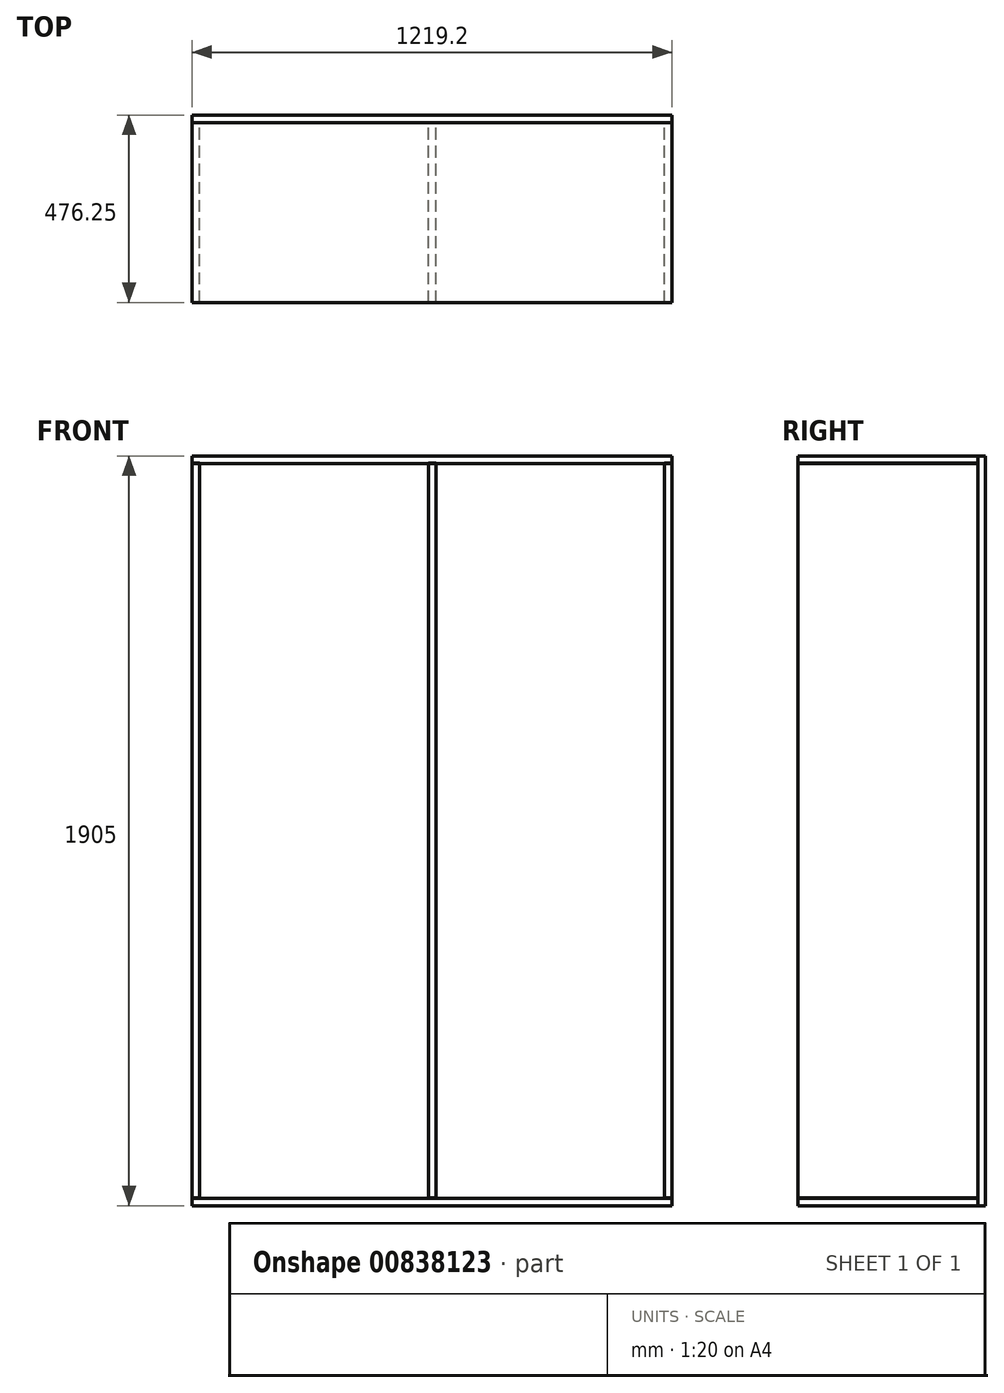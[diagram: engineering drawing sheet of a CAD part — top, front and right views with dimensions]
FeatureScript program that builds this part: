
annotation { "Feature Type Name" : "Feature", "Feature Type Description" : "" }
export const myFeature = defineFeature(function(context is Context, id is Id, definition is map)
    precondition{}
    {
        {
            var Q0;
            Q0=qCreatedBy(makeId("Front.planeOp"),FACE);
            var sketch = newSketch(context, id + "F0", { "sketchPlane" : qUnion([Q0])});
            skLineSegment(sketch, "E0.bottom", {"start": v(0, 0) * mm, "end": v(1219.2, 0) * mm});
            skLineSegment(sketch, "E0.top", {"start": v(0, 1905) * mm, "end": v(1219.2, 1905) * mm});
            skLineSegment(sketch, "E0.left", {"start": v(0, 0) * mm, "end": v(0, 1905) * mm});
            skLineSegment(sketch, "E0.right", {"start": v(1219.2, 0) * mm, "end": v(1219.2, 1905) * mm});
            skSolve(sketch);
        }
        {
            var Q0;
            Q0 = qSketchRegion(id + "F0", true);
            extrude(context, id + "F1", {"entities" : qUnion([Q0]), "depth" : 19.05 * mm, "offsetDistance" : 25.4 * mm});
        }
        {
            var Q0;
            Q0=makeQuery(id+"F1.opExtrude","CAP_FACE",FACE,{"disambiguationData":[OSD([sQuery(id+"F0.wireOp",EDGE,"E0.bottom"),sQuery(id+"F0.wireOp",EDGE,"E0.top"),sQuery(id+"F0.wireOp",EDGE,"E0.left"),sQuery(id+"F0.wireOp",EDGE,"E0.right")])],"isStart":false});
            var sketch = newSketch(context, id + "F2", { "sketchPlane" : qUnion([Q0])});
            skLineSegment(sketch, "E1.bottom", {"start": v(0, 1905) * mm, "end": v(1219.2, 1905) * mm});
            skLineSegment(sketch, "E1.top", {"start": v(0, 1885.95) * mm, "end": v(1219.2, 1885.95) * mm});
            skLineSegment(sketch, "E1.left", {"start": v(0, 1905) * mm, "end": v(0, 1885.95) * mm});
            skLineSegment(sketch, "E1.right", {"start": v(1219.2, 1905) * mm, "end": v(1219.2, 1885.95) * mm});
            skSolve(sketch);
        }
        {
            var Q0;
            Q0 = qSketchRegion(id + "F2", true);
            extrude(context, id + "F3", {"entities" : qUnion([Q0]), "depth" : 457.2 * mm, "offsetDistance" : 25.4 * mm});
        }
        {
            var Q0;
            Q0=makeQuery(id+"F3.opExtrude","SWEPT_BODY",BODY,{"disambiguationData":[OSD([sQuery(id+"F2.wireOp",EDGE,"E1.bottom"),sQuery(id+"F2.wireOp",EDGE,"E1.top"),sQuery(id+"F2.wireOp",EDGE,"E1.left"),sQuery(id+"F2.wireOp",EDGE,"E1.right")])]});
            var Q1;
            Q1=makeQuery(id+"F3.opExtrude","SWEPT_FACE",FACE,{"disambiguationData":[OSD([sQuery(id+"F2.wireOp",EDGE,"E1.top")])]});
            transform(context, id + "F4", {"entities" : qUnion([Q0]), "transformType" : TransformType.TRANSLATION_DISTANCE, "transformDirection" : qUnion([Q1]), "distance" : 1885.95 * mm, "makeCopy" : true});
        }
        {
            var Q0;
            Q0=makeQuery(id+"F1.opExtrude","CAP_FACE",FACE,{"disambiguationData":[OSD([sQuery(id+"F0.wireOp",EDGE,"E0.bottom"),sQuery(id+"F0.wireOp",EDGE,"E0.top"),sQuery(id+"F0.wireOp",EDGE,"E0.left"),sQuery(id+"F0.wireOp",EDGE,"E0.right")])],"isStart":false});
            var sketch = newSketch(context, id + "F5", { "sketchPlane" : qUnion([Q0])});
            skLineSegment(sketch, "E2.bottom", {"start": v(0, 1886.66) * mm, "end": v(19.05, 1886.66) * mm});
            skLineSegment(sketch, "E2.top", {"start": v(0, 19.76) * mm, "end": v(19.05, 19.76) * mm});
            skLineSegment(sketch, "E2.left", {"start": v(0, 1886.66) * mm, "end": v(0, 19.76) * mm});
            skLineSegment(sketch, "E2.right", {"start": v(19.05, 1886.66) * mm, "end": v(19.05, 19.76) * mm});
            skSolve(sketch);
        }
        {
            var Q0;
            Q0=makeQuery(id+"F5.imprint","IMPRINT",FACE,{"disambiguationData":[TD([[makeQuery(id+"F5.imprint","IMPRINT",EDGE,{"derivedFrom":sQuery(id+"F5.wireOp",EDGE,"E2.bottom")}),-1.0]])]});
            extrude(context, id + "F6", {"entities" : qUnion([Q0]), "depth" : 457.2 * mm, "offsetDistance" : 25.4 * mm});
        }
        {
            var Q0;
            Q0=makeQuery(id+"F6.opExtrude","SWEPT_BODY",BODY,{"disambiguationData":[OSD([sQuery(id+"F5.wireOp",EDGE,"E2.bottom"),sQuery(id+"F5.wireOp",EDGE,"E2.top"),sQuery(id+"F5.wireOp",EDGE,"E2.left"),sQuery(id+"F5.wireOp",EDGE,"E2.right")])]});
            var Q1;
            Q1=makeQuery(id+"F6.opExtrude","SWEPT_FACE",FACE,{"disambiguationData":[OSD([sQuery(id+"F5.wireOp",EDGE,"E2.right")])]});
            transform(context, id + "F7", {"entities" : qUnion([Q0]), "transformType" : TransformType.TRANSLATION_DISTANCE, "transformDirection" : qUnion([Q1]), "distance" : 600.07 * mm, "makeCopy" : true});
        }
        {
            var Q0;
            Q0=makeQuery(id+"F7.opPattern","COPY",BODY,{"derivedFrom":makeQuery(id+"F6.opExtrude","SWEPT_BODY",BODY,{"disambiguationData":[OSD([sQuery(id+"F5.wireOp",EDGE,"E2.bottom"),sQuery(id+"F5.wireOp",EDGE,"E2.top"),sQuery(id+"F5.wireOp",EDGE,"E2.left"),sQuery(id+"F5.wireOp",EDGE,"E2.right")])]}),"instanceName":"1"});
            var Q1;
            Q1=makeQuery(id+"F7.opPattern","COPY",FACE,{"derivedFrom":makeQuery(id+"F6.opExtrude","SWEPT_FACE",FACE,{"disambiguationData":[OSD([sQuery(id+"F5.wireOp",EDGE,"E2.right")])]}),"instanceName":"1"});
            transform(context, id + "F8", {"entities" : qUnion([Q0]), "transformType" : TransformType.TRANSLATION_DISTANCE, "transformDirection" : qUnion([Q1]), "distance" : 600.07 * mm, "makeCopy" : true});
        }
    });
